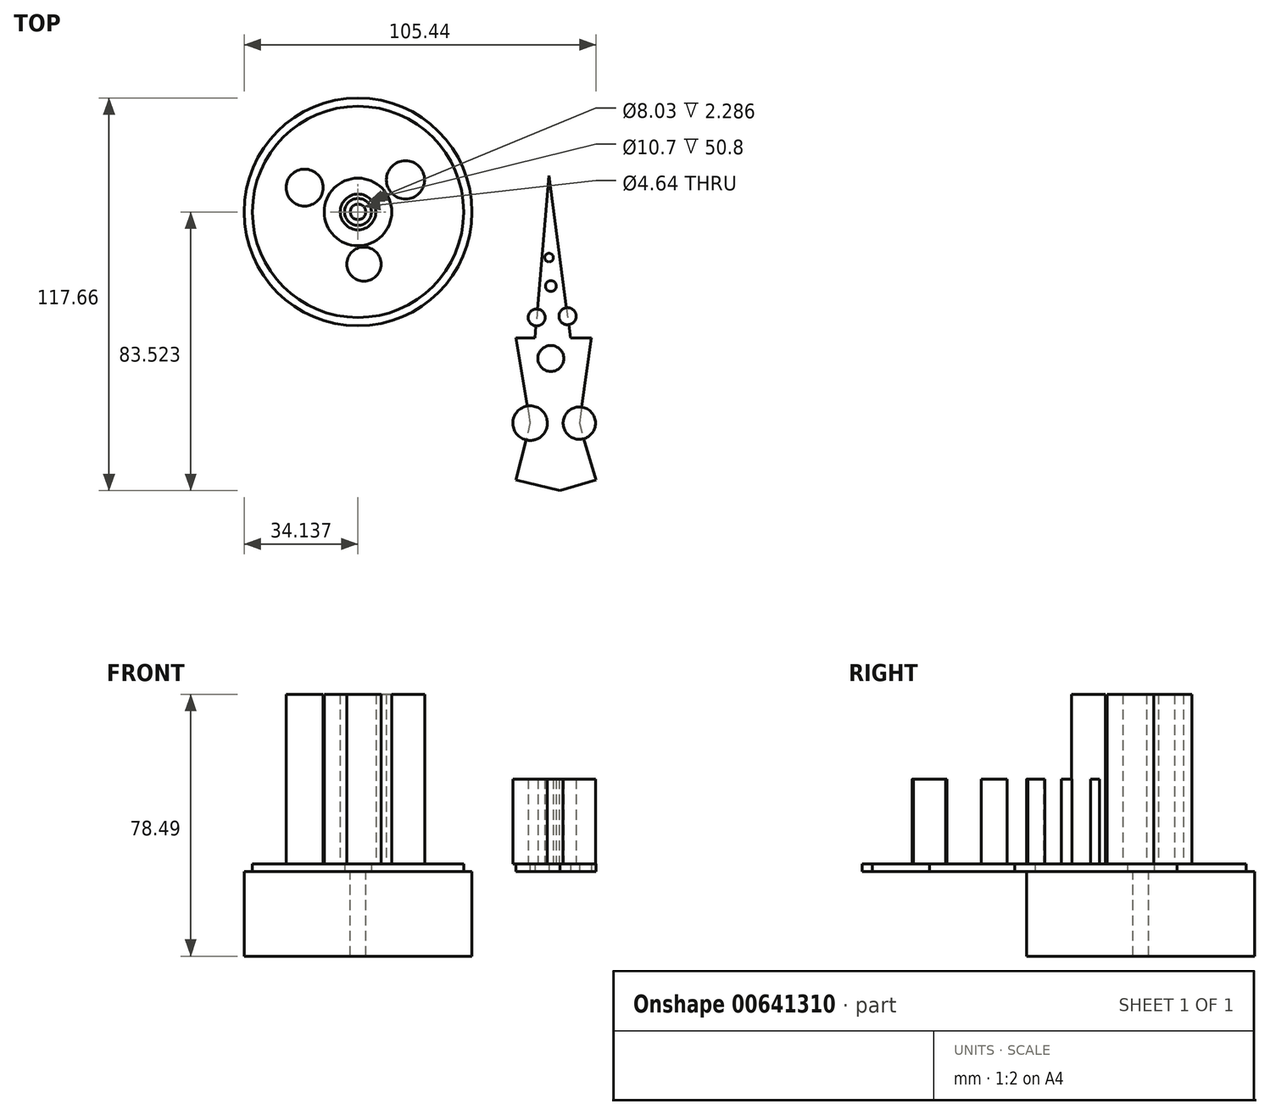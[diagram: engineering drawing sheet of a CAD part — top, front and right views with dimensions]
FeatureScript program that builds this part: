
annotation { "Feature Type Name" : "Feature", "Feature Type Description" : "" }
export const myFeature = defineFeature(function(context is Context, id is Id, definition is map)
    precondition{}
    {
        {
            var Q0;
            Q0=qCreatedBy(makeId("Top.planeOp"),FACE);
            var sketch = newSketch(context, id + "F0", { "sketchPlane" : qUnion([Q0])});
            skCircle(sketch, "E0", {"center": v(-30.5, 37.78) * mm, "radius": 31.65 * mm});
            skCircle(sketch, "E1", {"center": v(-30.5, 37.78) * mm, "radius": 4.02 * mm});
            skSolve(sketch);
        }
        {
            var Q0;
            Q0 = qSketchRegion(id + "F0", true);
            extrude(context, id + "F1", {"entities" : qUnion([Q0]), "depth" : 2.3 * mm, "offsetDistance" : 25.4 * mm});
        }
        {
            var Q0;
            Q0=makeQuery(id+"F1.opExtrude","CAP_FACE",FACE,{"disambiguationData":[OSD([sQuery(id+"F0.wireOp",EDGE,"E0")])],"isStart":false});
            var sketch = newSketch(context, id + "F2", { "sketchPlane" : qUnion([Q0])});
            skCircle(sketch, "E2", {"center": v(-30.5, 37.78) * mm, "radius": 10.1 * mm});
            skCircle(sketch, "E3", {"center": v(-30.5, 37.78) * mm, "radius": 5.35 * mm});
            skCircle(sketch, "E4", {"center": v(-46.5, 45.07) * mm, "radius": 5.54 * mm});
            skCircle(sketch, "E5", {"center": v(-16.27, 47.38) * mm, "radius": 5.73 * mm});
            skCircle(sketch, "E6", {"center": v(-28.71, 22.14) * mm, "radius": 5.12 * mm});
            skSolve(sketch);
        }
        {
            var Q0;
            Q0 = qSketchRegion(id + "F2", true);
            extrude(context, id + "F3", {"entities" : qUnion([Q0]), "operationType" : NewBodyOperationType.ADD, "depth" : 50.8 * mm, "offsetDistance" : 25.4 * mm});
        }
        {
            var Q0;
            Q0=makeQuery(id+"F1.opExtrude","CAP_FACE",FACE,{"disambiguationData":[OSD([sQuery(id+"F0.wireOp",EDGE,"E0"),sQuery(id+"F0.wireOp",EDGE,"E1")])],"isStart":true});
            var sketch = newSketch(context, id + "F4", { "sketchPlane" : qUnion([Q0])});
            skCircle(sketch, "E7", {"center": v(-30.5, -37.78) * mm, "radius": 34.14 * mm});
            skCircle(sketch, "E8", {"center": v(-30.5, -37.78) * mm, "radius": 2.32 * mm});
            skSolve(sketch);
        }
        {
            var Q0;
            Q0 = qSketchRegion(id + "F4", true);
            extrude(context, id + "F5", {"entities" : qUnion([Q0]), "operationType" : NewBodyOperationType.ADD, "depth" : 25.4 * mm, "offsetDistance" : 25.4 * mm});
        }
        {
            var Q0;
            Q0=qCreatedBy(makeId("Top.planeOp"),FACE);
            var sketch = newSketch(context, id + "F6", { "sketchPlane" : qUnion([Q0])});
            skLineSegment(sketch, "E9", {"start": v(26.76, 48.63) * mm, "end": v(22.5, 0) * mm});
            skLineSegment(sketch, "E10", {"start": v(26.76, 48.63) * mm, "end": v(33.16, 0) * mm});
            skLineSegment(sketch, "E11", {"start": v(16.8, 0) * mm, "end": v(39.38, 0) * mm});
            skLineSegment(sketch, "E12", {"start": v(16.8, 0) * mm, "end": v(21.07, -25.51) * mm});
            skLineSegment(sketch, "E13", {"start": v(21.07, -25.51) * mm, "end": v(16.8, -42.58) * mm});
            skLineSegment(sketch, "E14", {"start": v(39.38, 0) * mm, "end": v(35.83, -25.51) * mm});
            skLineSegment(sketch, "E15", {"start": v(35.83, -25.51) * mm, "end": v(40.8, -42.58) * mm});
            skLineSegment(sketch, "E16", {"start": v(40.8, -42.58) * mm, "end": v(30, -45.74) * mm});
            skLineSegment(sketch, "E17", {"start": v(16.8, -42.58) * mm, "end": v(30, -45.74) * mm});
            skSolve(sketch);
        }
        {
            var Q0;
            Q0 = qSketchRegion(id + "F6", true);
            extrude(context, id + "F7", {"entities" : qUnion([Q0]), "depth" : 2.3 * mm, "offsetDistance" : 25.4 * mm});
        }
        {
            var Q0;
            Q0=makeQuery(id+"F7.opExtrude","CAP_FACE",FACE,{"disambiguationData":[OSD([sQuery(id+"F6.wireOp",EDGE,"E9"),sQuery(id+"F6.wireOp",EDGE,"E10"),sQuery(id+"F6.wireOp",EDGE,"E11"),sQuery(id+"F6.wireOp",EDGE,"E12"),sQuery(id+"F6.wireOp",EDGE,"E13"),sQuery(id+"F6.wireOp",EDGE,"E14"),sQuery(id+"F6.wireOp",EDGE,"E15"),sQuery(id+"F6.wireOp",EDGE,"E16"),sQuery(id+"F6.wireOp",EDGE,"E17")])],"isStart":false});
            var sketch = newSketch(context, id + "F8", { "sketchPlane" : qUnion([Q0])});
            skCircle(sketch, "E18", {"center": v(27.3, 15.56) * mm, "radius": 1.61 * mm});
            skCircle(sketch, "E19", {"center": v(23.03, 6.16) * mm, "radius": 2.55 * mm});
            skCircle(sketch, "E20", {"center": v(32.3, 6.52) * mm, "radius": 2.58 * mm});
            skCircle(sketch, "E21", {"center": v(26.76, 24.1) * mm, "radius": 1.28 * mm});
            skCircle(sketch, "E22", {"center": v(27.3, -6.13) * mm, "radius": 3.88 * mm});
            skCircle(sketch, "E23", {"center": v(21.07, -25.51) * mm, "radius": 5.18 * mm});
            skCircle(sketch, "E24", {"center": v(35.83, -25.51) * mm, "radius": 4.85 * mm});
            skSolve(sketch);
        }
        {
            var Q0;
            Q0 = qSketchRegion(id + "F8", true);
            extrude(context, id + "F9", {"entities" : qUnion([Q0]), "operationType" : NewBodyOperationType.ADD, "depth" : 25.4 * mm, "offsetDistance" : 25.4 * mm});
        }
    });
